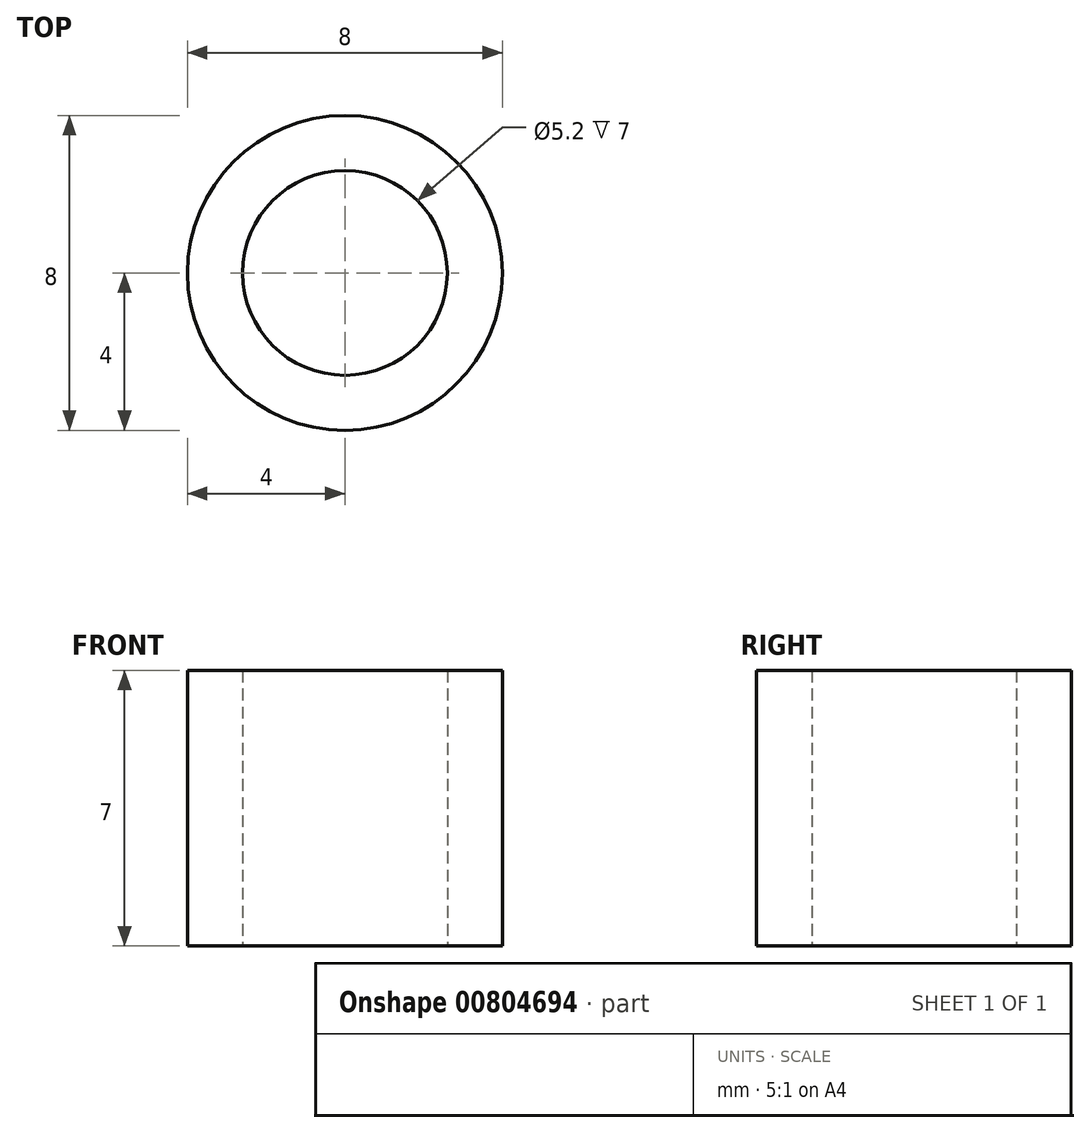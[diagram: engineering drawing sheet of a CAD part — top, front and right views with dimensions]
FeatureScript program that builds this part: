
annotation { "Feature Type Name" : "Feature", "Feature Type Description" : "" }
export const myFeature = defineFeature(function(context is Context, id is Id, definition is map)
    precondition{}
    {
        {
            var Q0;
            Q0=qCreatedBy(makeId("Top.planeOp"),FACE);
            var sketch = newSketch(context, id + "F0", { "sketchPlane" : qUnion([Q0])});
            skCircle(sketch, "E0", {"center": v(0, 0) * mm, "radius": 4 * mm});
            skCircle(sketch, "E1", {"center": v(0, 0) * mm, "radius": 2.6 * mm});
            skSolve(sketch);
        }
        {
            var Q0;
            Q0=qSketchRegion(id+"F0",true);
            extrude(context, id + "F1", {"entities" : qUnion([Q0]), "depth" : 7 * mm, "offsetDistance" : 25 * mm});
        }
    });
